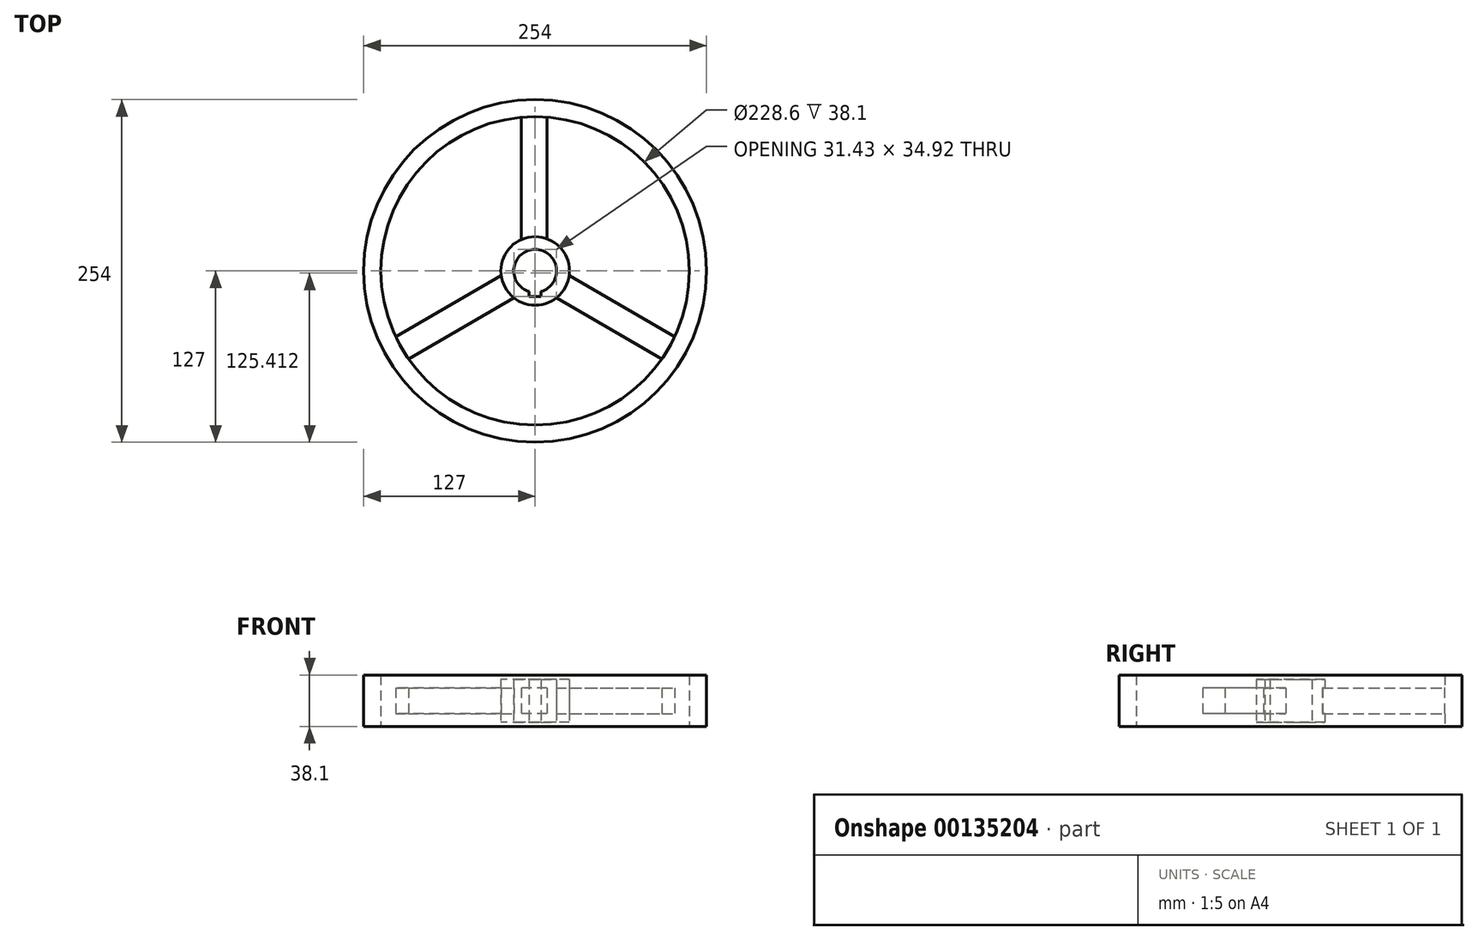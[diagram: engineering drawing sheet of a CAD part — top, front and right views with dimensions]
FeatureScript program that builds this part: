
annotation { "Feature Type Name" : "Feature", "Feature Type Description" : "" }
export const myFeature = defineFeature(function(context is Context, id is Id, definition is map)
    precondition{}
    {
        {
            var Q0;
            Q0=qCreatedBy(makeId("Top.planeOp"),FACE);
            var sketch = newSketch(context, id + "F0", { "sketchPlane" : qUnion([Q0])});
            skArc(sketch, "E0", {"start": v(4.45, -15.24) * mm, "mid": v(0, 15.88) * mm, "end": v(-4.45, -15.24) * mm});
            skCircle(sketch, "E1", {"center": v(0, 0) * mm, "radius": 25.4 * mm});
            skCircle(sketch, "E2", {"center": v(0, 0) * mm, "radius": 114.3 * mm});
            skCircle(sketch, "E3", {"center": v(0, 0) * mm, "radius": 127 * mm});
            skLineSegment(sketch, "E4", {"start": v(-10.16, 23.28) * mm, "end": v(-10.16, 113.85) * mm});
            skLineSegment(sketch, "E5", {"start": v(8.9, 23.8) * mm, "end": v(8.9, 113.95) * mm});
            skLineSegment(sketch, "E6", {"start": v(-25.15, -3.52) * mm, "end": v(-103.4, -48.7) * mm});
            skLineSegment(sketch, "E7", {"start": v(-93.88, -65.2) * mm, "end": v(-15.63, -20.02) * mm});
            skLineSegment(sketch, "E8", {"start": v(15.63, -20.02) * mm, "end": v(93.88, -65.2) * mm});
            skLineSegment(sketch, "E9", {"start": v(25.15, -3.52) * mm, "end": v(103.4, -48.7) * mm});
            skLineSegment(sketch, "E10", {"start": v(-4.45, -15.24) * mm, "end": v(-4.45, -19.05) * mm});
            skLineSegment(sketch, "E11", {"start": v(-4.45, -19.05) * mm, "end": v(4.45, -19.05) * mm});
            skLineSegment(sketch, "E12", {"start": v(4.44, -19.05) * mm, "end": v(4.44, -15.24) * mm});
            skSolve(sketch);
        }
        {
            var Q0;
            Q0=makeQuery(id+"F0.imprint","IMPRINT",FACE,{"disambiguationData":[TD([[makeQuery(id+"F0.imprint","IMPRINT",EDGE,{"derivedFrom":sQuery(id+"F0.wireOp",EDGE,"E3")}),1.0]])]});
            extrude(context, id + "F1", {"entities" : qUnion([Q0]), "endBound" : BoundingType.SYMMETRIC, "depth" : 38.1 * mm});
        }
        {
            var Q0;
            Q0 = qSketchRegion(id + "F0", true);
            var Q1;
            {var subQ0=sQuery(id+"F0.wireOp",EDGE,"E4");Q1=makeQuery(id+"F0.imprint","IMPRINT",FACE,{"disambiguationData":[TD([[makeQuery(id+"F0.imprint","IMPRINT",EDGE,{"derivedFrom":subQ0}),-1.0]])]});}
            var Q2;
            {var subQ0=sQuery(id+"F0.wireOp",EDGE,"E6");Q2=makeQuery(id+"F0.imprint","IMPRINT",FACE,{"disambiguationData":[TD([[makeQuery(id+"F0.imprint","IMPRINT",EDGE,{"derivedFrom":subQ0}),1.0]])]});}
            var Q3;
            {var subQ0=sQuery(id+"F0.wireOp",EDGE,"E8");Q3=makeQuery(id+"F0.imprint","IMPRINT",FACE,{"disambiguationData":[TD([[makeQuery(id+"F0.imprint","IMPRINT",EDGE,{"derivedFrom":subQ0}),1.0]])]});}
            extrude(context, id + "F2", {"entities" : qUnion([Q0, Q1, Q2, Q3]), "operationType" : NewBodyOperationType.ADD, "endBound" : BoundingType.SYMMETRIC, "depth" : 19.05 * mm});
        }
        {
            var Q0;
            Q0=makeQuery(id+"F0.imprint","IMPRINT",FACE,{"disambiguationData":[TD([[makeQuery(id+"F0.imprint","IMPRINT",EDGE,{"derivedFrom":sQuery(id+"F0.wireOp",EDGE,"E0")}),-1.0]])]});
            extrude(context, id + "F3", {"entities" : qUnion([Q0]), "operationType" : NewBodyOperationType.ADD, "endBound" : BoundingType.SYMMETRIC, "depth" : 31.75 * mm});
        }
    });
